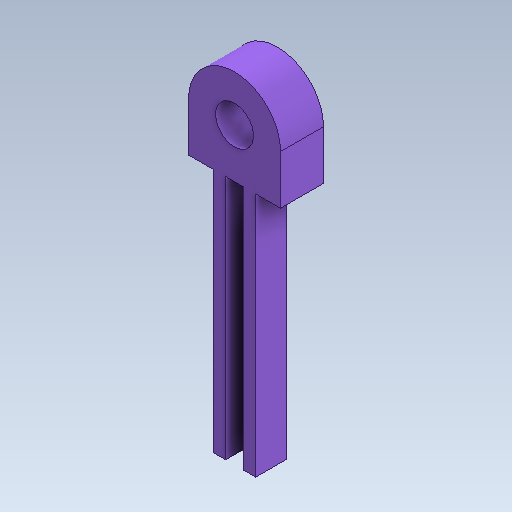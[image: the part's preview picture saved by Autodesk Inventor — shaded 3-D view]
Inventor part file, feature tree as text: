
AUTODESK INVENTOR PART (.ipt)
format: ipt  version: 2020 (Build 240168000, 168)  size: 134,144 bytes
history: native  units: in
note: dims shown in document units (in); Inventor stores cm internally (conversion verified against a paired STEP export)
features: sketch x8, other x3
ambient origin geometry x8: Origin, YZ Plane, XZ Plane, XY Plane, X Axis, Y Axis, Z Axis, Center Point
bodies: Solid1 (feature_tree)
feature tree (11):
  other  "PistonBot.ipt"
  other  "Solid1::PistonBot.ipt"
  other  "TaggingFeature1"
  sketch  "Sketch1"  dims[d0=0.3937in]
  sketch  "Sketch4"
  sketch  "Sketch5"
  sketch  "Sketch6"
  sketch  "Sketch7"
  sketch  "Sketch8"
  sketch  "Sketch9"
  sketch  "Sketch11"
